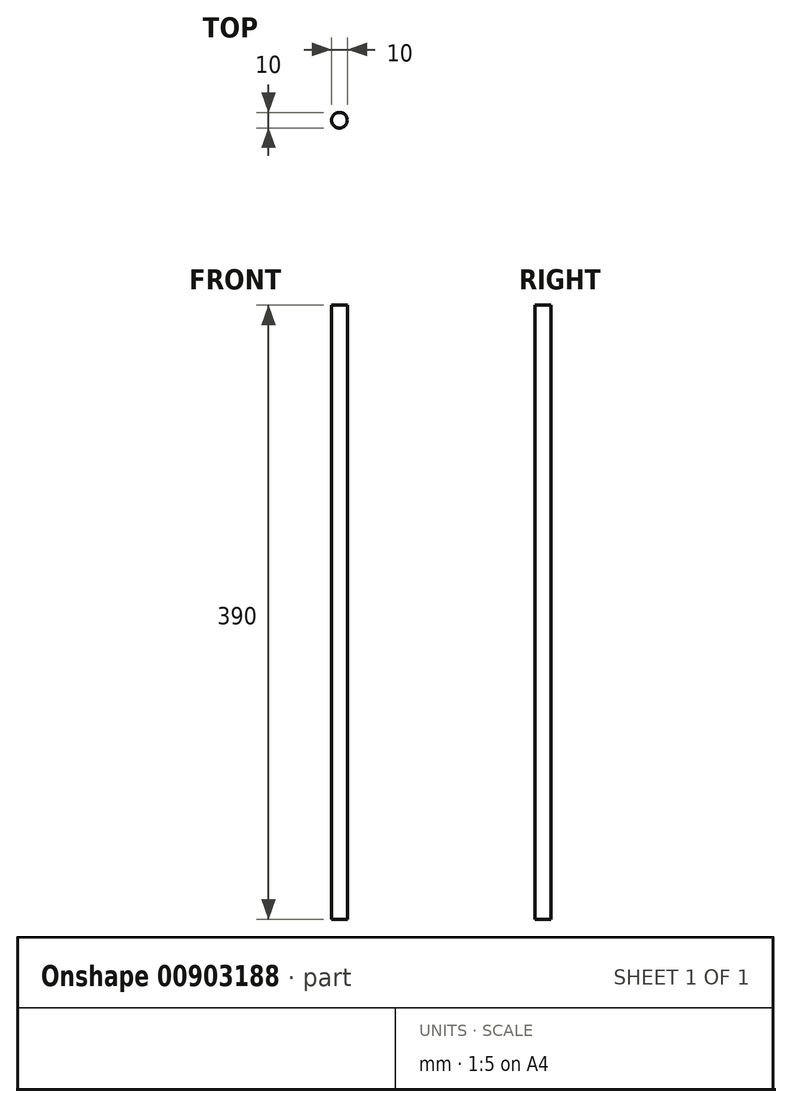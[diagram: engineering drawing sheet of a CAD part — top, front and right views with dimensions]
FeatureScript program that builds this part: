
annotation { "Feature Type Name" : "Feature", "Feature Type Description" : "" }
export const myFeature = defineFeature(function(context is Context, id is Id, definition is map)
    precondition{}
    {
        {
            var Q0;
            Q0=qCreatedBy(makeId("Front.planeOp"),FACE);
            var sketch = newSketch(context, id + "F0", { "sketchPlane" : qUnion([Q0])});
            skLineSegment(sketch, "E0.bottom", {"start": v(0, 0) * mm, "end": v(5, 0) * mm});
            skLineSegment(sketch, "E0.top", {"start": v(0, -390) * mm, "end": v(5, -390) * mm});
            skLineSegment(sketch, "E0.left", {"start": v(0, 0) * mm, "end": v(0, -390) * mm});
            skLineSegment(sketch, "E0.right", {"start": v(5, 0) * mm, "end": v(5, -390) * mm});
            skSolve(sketch);
        }
        {
            var Q0;
            Q0=makeQuery(id+"F0.imprint","IMPRINT",FACE,{"disambiguationData":[TD([[makeQuery(id+"F0.imprint","IMPRINT",EDGE,{"derivedFrom":sQuery(id+"F0.wireOp",EDGE,"E0.bottom")}),-1.0]])]});
            var Q1;
            Q1=sQuery(id+"F0.wireOp",EDGE,"E0.left");
            revolve(context, id + "F1", {"surfaceOperationType" : NewSurfaceOperationType.NEW, "entities" : qUnion([Q0]), "axis" : qUnion([Q1]), "revolveType" : RevolveType.FULL});
        }
    });
